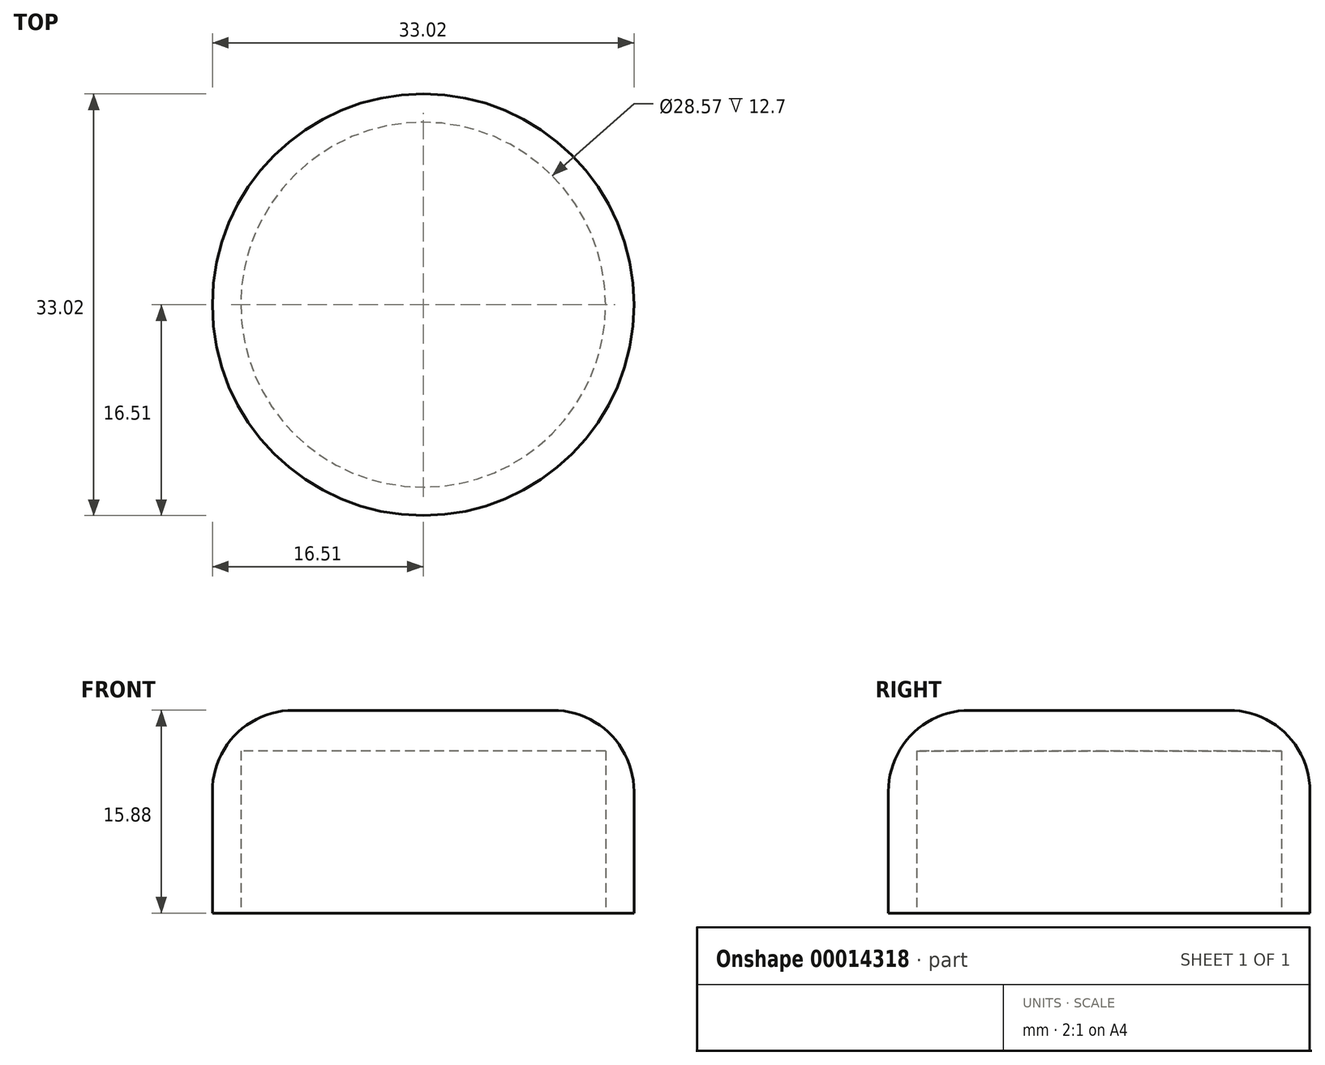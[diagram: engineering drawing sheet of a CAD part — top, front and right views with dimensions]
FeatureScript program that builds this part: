
annotation { "Feature Type Name" : "Feature", "Feature Type Description" : "" }
export const myFeature = defineFeature(function(context is Context, id is Id, definition is map)
    precondition{}
    {
        {
            var Q0;
            Q0=qCreatedBy(makeId("Top.planeOp"),FACE);
            var sketch = newSketch(context, id + "F0", { "sketchPlane" : qUnion([Q0])});
            skCircle(sketch, "E0", {"center": v(0, 0) * mm, "radius": 14.29 * mm});
            skCircle(sketch, "E1", {"center": v(0, 0) * mm, "radius": 16.51 * mm});
            skSolve(sketch);
        }
        {
            var Q0;
            Q0=makeQuery(id+"F0.imprint","IMPRINT",FACE,{"disambiguationData":[TD([[makeQuery(id+"F0.imprint","IMPRINT",EDGE,{"derivedFrom":sQuery(id+"F0.wireOp",EDGE,"E0")}),-1.0]])]});
            extrude(context, id + "F1", {"entities" : qUnion([Q0]), "depth" : 12.7 * mm});
        }
        {
            var Q0;
            Q0=makeQuery(id+"F1.opExtrude","CAP_FACE",FACE,{"disambiguationData":[OSD([sQuery(id+"F0.wireOp",EDGE,"E0"),sQuery(id+"F0.wireOp",EDGE,"E1")])],"isStart":false});
            var sketch = newSketch(context, id + "F2", { "sketchPlane" : qUnion([Q0])});
            skCircle(sketch, "E2", {"center": v(0, 0) * mm, "radius": 16.51 * mm});
            skSolve(sketch);
        }
        {
            var Q0;
            Q0=makeQuery(id+"F2.imprint","IMPRINT",FACE,{"disambiguationData":[TD([[makeQuery(id+"F2.imprint","IMPRINT",EDGE,{"derivedFrom":sQuery(id+"F2.wireOp",EDGE,"E2")}),1.0]])]});
            var Q1;
            Q1=makeQuery(id+"F2.imprint","IMPRINT",FACE,{"disambiguationData":[TD([[makeQuery(id+"F2.imprint","IMPRINT",EDGE,{"derivedFrom":makeQuery(id+"F1.opExtrude","CAP_EDGE",EDGE,{"disambiguationData":[OSD([sQuery(id+"F0.wireOp",EDGE,"E0")])],"isStart":false})}),1.0]])]});
            extrude(context, id + "F3", {"entities" : qUnion([Q0, Q1]), "operationType" : NewBodyOperationType.ADD, "depth" : 3.17 * mm});
        }
        {
            var Q0;
            Q0=makeQuery(id+"F3.opExtrude","CAP_EDGE",EDGE,{"disambiguationData":[OSD([sQuery(id+"F2.wireOp",EDGE,"E2")])],"isStart":false});
            fillet(context, id + "F4", {"entities" : qUnion([Q0]), "radius" : 6.35 * mm, "tangentPropagation" : true, "allowEdgeOverflow" : false});
        }
    });
